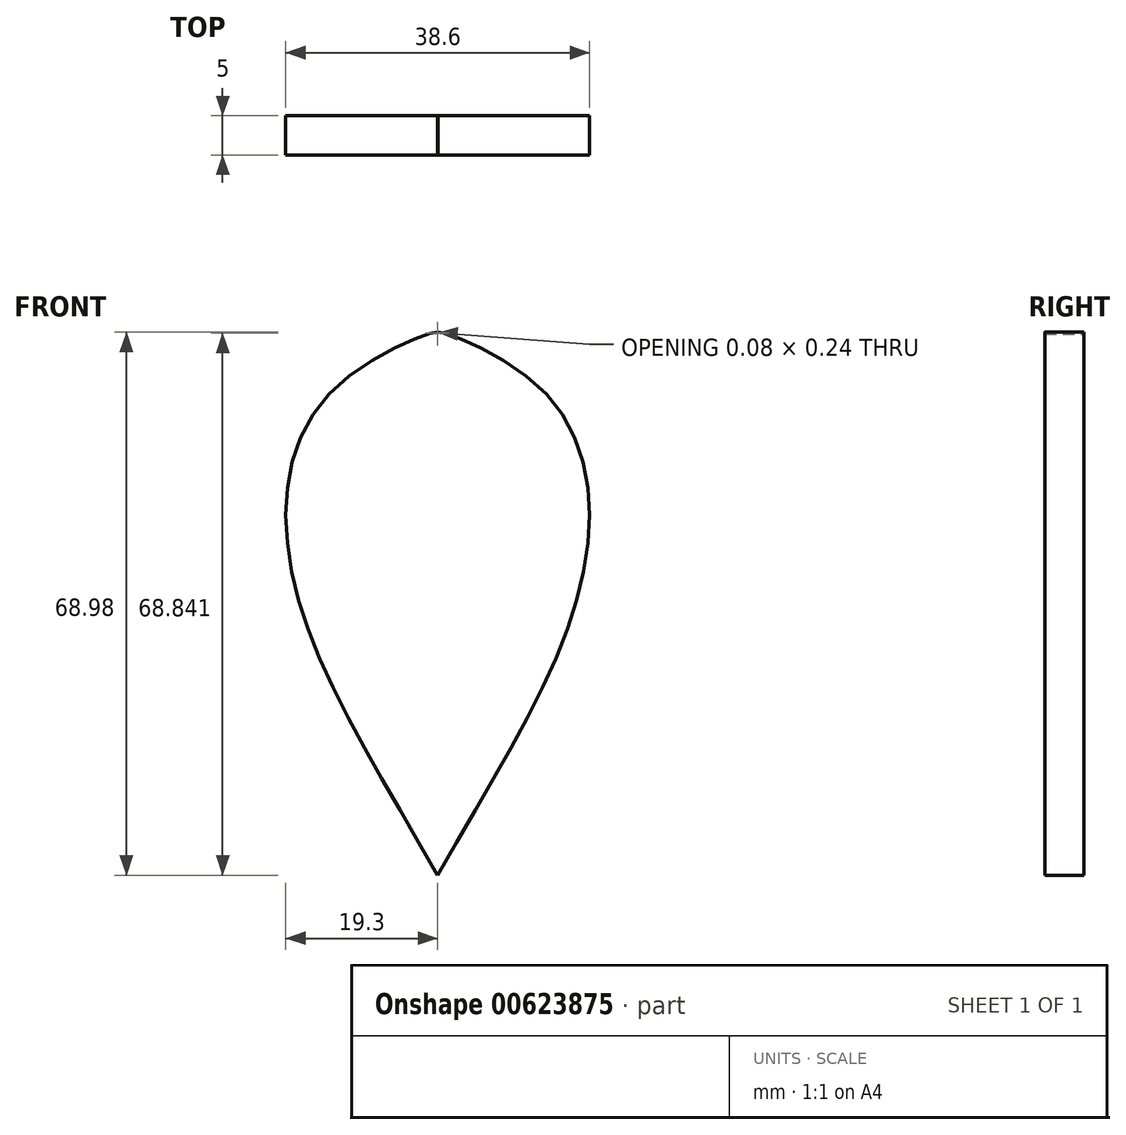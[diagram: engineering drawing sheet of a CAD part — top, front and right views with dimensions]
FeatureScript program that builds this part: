
annotation { "Feature Type Name" : "Feature", "Feature Type Description" : "" }
export const myFeature = defineFeature(function(context is Context, id is Id, definition is map)
    precondition{}
    {
        {
            var Q0;
            Q0=qCreatedBy(makeId("Front.planeOp"),FACE);
            var sketch = newSketch(context, id + "F0", { "sketchPlane" : qUnion([Q0])});
            skFitSpline(sketch, "E0", {"points": [v(0, 0) * mm, v(-18.37, 37.71) * mm, v(-13.25, 61.68) * mm, v(0, 68.96) * mm, v(0, 68.72) * mm], "startDerivative": vector(-57.74, 101.02) * mm, "endDerivative": vector(-3.23, -10.68) * mm});
            skFitSpline(sketch, "E1.MirrorCS", {"points": [v(0, 0) * mm, v(18.37, 37.71) * mm, v(13.25, 61.68) * mm, v(0, 68.96) * mm, v(0, 68.72) * mm], "startDerivative": vector(57.74, 101.02) * mm, "endDerivative": vector(3.23, -10.68) * mm});
            skLineSegment(sketch, "E2", {"start": v(-0.03, 68.97) * mm, "end": v(0.03, 68.97) * mm});
            skSolve(sketch);
        }
        {
            var Q0;
            Q0 = qSketchRegion(id + "F0", true);
            extrude(context, id + "F1", {"entities" : qUnion([Q0]), "depth" : 5 * mm, "offsetDistance" : 25 * mm});
        }
    });
